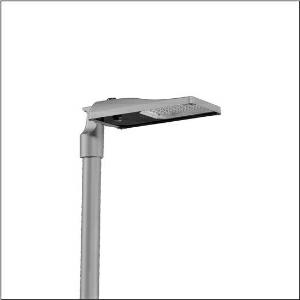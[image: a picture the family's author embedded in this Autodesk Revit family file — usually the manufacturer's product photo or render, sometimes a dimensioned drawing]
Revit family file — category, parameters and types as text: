
# Revit family: streetlight_sl_31_mini___stw1_0a_5xh6e31t08ga_7388
name_source: partatom
category: Lighting Fixtures
units: mm (PartAtom-declared; Revit-internal decimal feet)

## family parameters
Cut with Voids When Loaded = No
Host = Face
Light Source = No
Part Type = Normal
Room Calculation Point = No
Round Connector Dimension = Use Diameter
Shared = No

## types (1)
- --- (1 x LED, 5880 lm, 39.3 W, 3000K)
    Apparent Load = 39 VA
    CIE Flux Codes = 38 75 98 100 100
    Color Rendering = 70
    Color Temperature = 3000K
    Default Elevation = 1800 mm
    Description = Streetlight SL 31 mini D4i, Desk-Remote mast luminaire for post-top, side-entry; light control with lens of PMMA; light distribution: STW1.0a, direct asymmetric distribution, for standard-compliant lighting for roads and squares; LED: luminous flux: 5.880lm, light colour: 730, colour temperature: 3000K; luminous efficacy: 149,6lm/W; control: pre-setting: logarithmic dimming characteristic, flexible luminous flux parameterisation, time-dependent luminous flux control, constant luminous flux control, power reduction, intelligent temperature release in ECG and LED module, overheat protection; luminaire housing, of diecast aluminium, SITECO metallic grey (DB 702S), corrosivity category C5 high according to DIN EN ISO 12944; cover of toughened safety glass, transparent, opened without tools; mast flange of diecast aluminium, SITECO metallic grey (DB 702S), spigot size: 76/60mm, mast flange included unmounted; cable length: 6,5m, connection cable pre-assembled; mains connection: 220..240V, AC, 50/60Hz; power consumption (at start of service life): 39,3W / (at end of service life): 40,7W / (with reduced operation 50%): 18,1W; protection rating (complete): IP66; insulation class (complete): insulation class II (safety insulation); impact resistance: IK09; certification: CE, ENEC, ENEC+, VDE, UKCA, ZD4i; permissible operating ambient temperature for outdoor applications: -40..+50°C; packaging unit: 1 piece

Light Distribution: STW1.0a
    Height = 76 mm
    Lamp = 1 x LED
    Lamp Light Flux = 5880 lm
    Lamp Power = 39.3 W
    Lamp count = 1
    Length = 547 mm
    Luminous efficacy = 150 lm/W
    Manufacturer = Siteco
    ModVariant = No
    Model = 5XH6E31T08GA
    Number of Poles = 1
    OnlyDefault = Yes
    Power Factor = 1
    Product Name = Streetlight SL 31 mini | STW1.0a
    Product group = mast luminaire | pylon top
    ProductGroupID = 6100
    Protection Class = Protection class II
    Protection Degree = IP 66
    RLX_Detail_Level = 1
    RLX_Emergency_Light_Flux = 0 lm
    RLX_Emergency_Type = 0
    RLX_Emergency_Type_DB = No
    RlxData = <blob elided: 40025 chars, md5=663ff0e8>
    Socket = socket
    Standby Power = 0 W
    System Light Flux = 5880 lm
    System Power = 39 W
    Type Comments = factory setting: luminous flux: 100 % | dim-lin: 254 | 798 mA
    Type Image = l_1300332.jpg
    URL = http://relux.com
    VarID = @adj_060235
    Voltage = 0 V
    Weight = 0.00 kg
    Width = 265 mm

## geometry (parser evidence)
native form markers: Blend x4, Sweep x10
no freeform markers — native parametric forms only
